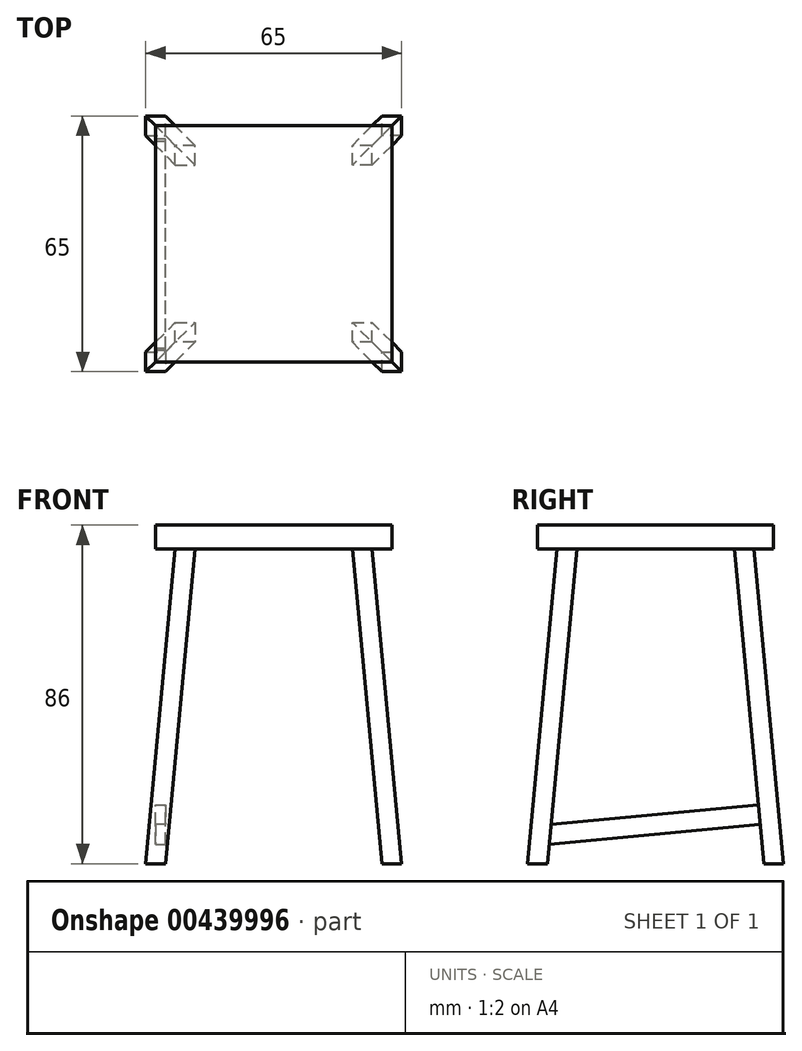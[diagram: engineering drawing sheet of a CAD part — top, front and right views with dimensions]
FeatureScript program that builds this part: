
annotation { "Feature Type Name" : "Feature", "Feature Type Description" : "" }
export const myFeature = defineFeature(function(context is Context, id is Id, definition is map)
    precondition{}
    {
        {
            var Q0;
            Q0=qCreatedBy(makeId("Top.planeOp"),FACE);
            var sketch = newSketch(context, id + "F0", { "sketchPlane" : qUnion([Q0])});
            skLineSegment(sketch, "E0.bottom", {"start": v(30, 30) * mm, "end": v(-30, 30) * mm});
            skLineSegment(sketch, "E0.top", {"start": v(30, -30) * mm, "end": v(-30, -30) * mm});
            skLineSegment(sketch, "E0.left", {"start": v(30, 30) * mm, "end": v(30, -30) * mm});
            skLineSegment(sketch, "E0.right", {"start": v(-30, 30) * mm, "end": v(-30, -30) * mm});
            skPoint(sketch, "E0.middle", {"position": v(0, 0) * mm});
            skSolve(sketch);
        }
        {
            var Q0;
            Q0=makeQuery(id+"F0.imprint","IMPRINT",FACE,{"disambiguationData":[TD([[makeQuery(id+"F0.imprint","IMPRINT",EDGE,{"derivedFrom":sQuery(id+"F0.wireOp",EDGE,"E0.bottom")}),1.0]])]});
            extrude(context, id + "F1", {"entities" : qUnion([Q0]), "depth" : 6 * mm});
        }
        {
            var Q0;
            Q0=makeQuery(id+"F1.opExtrude","CAP_FACE",FACE,{"disambiguationData":[OSD([sQuery(id+"F0.wireOp",EDGE,"E0.bottom"),sQuery(id+"F0.wireOp",EDGE,"E0.top"),sQuery(id+"F0.wireOp",EDGE,"E0.left"),sQuery(id+"F0.wireOp",EDGE,"E0.right")])],"isStart":true});
            var sketch = newSketch(context, id + "F2", { "sketchPlane" : qUnion([Q0])});
            skLineSegment(sketch, "E1.bottom", {"start": v(25, 25) * mm, "end": v(-25, 25) * mm});
            skLineSegment(sketch, "E1.top", {"start": v(25, -25) * mm, "end": v(-25, -25) * mm});
            skLineSegment(sketch, "E1.left", {"start": v(25, 25) * mm, "end": v(25, -25) * mm});
            skLineSegment(sketch, "E1.right", {"start": v(-25, 25) * mm, "end": v(-25, -25) * mm});
            skPoint(sketch, "E1.middle", {"position": v(0, 0) * mm});
            skLineSegment(sketch, "E2", {"start": v(-20, 25) * mm, "end": v(-20, 20) * mm});
            skLineSegment(sketch, "E3", {"start": v(-20, 20) * mm, "end": v(-25, 20) * mm});
            skLineSegment(sketch, "E4", {"start": v(-25, -20) * mm, "end": v(-20, -20) * mm});
            skLineSegment(sketch, "E5", {"start": v(-20, -20) * mm, "end": v(-20, -25) * mm});
            skLineSegment(sketch, "E6", {"start": v(25, 20) * mm, "end": v(20, 20) * mm});
            skLineSegment(sketch, "E7", {"start": v(20, 20) * mm, "end": v(20, 25) * mm});
            skLineSegment(sketch, "E8", {"start": v(25, -20) * mm, "end": v(20, -20) * mm});
            skLineSegment(sketch, "E9", {"start": v(20, -20) * mm, "end": v(20, -25) * mm});
            skSolve(sketch);
        }
        {
            var Q0;
            Q0=qCreatedBy(makeId("Top.planeOp"),FACE);
            cPlane(context, id + "F3", {"entities" : qUnion([Q0]), "cplaneType" : CPlaneType.OFFSET, "offset" : 80 * mm, "oppositeDirection" : true, "width" : 150 * mm, "height" : 150 * mm});
        }
        {
            var Q0;
            Q0=qCreatedBy(id+"F3.planeOp",FACE);
            var sketch = newSketch(context, id + "F4", { "sketchPlane" : qUnion([Q0])});
            skLineSegment(sketch, "E10.bottom", {"start": v(-32.5, 32.5) * mm, "end": v(32.5, 32.5) * mm});
            skLineSegment(sketch, "E10.top", {"start": v(-32.5, -32.5) * mm, "end": v(32.5, -32.5) * mm});
            skLineSegment(sketch, "E10.left", {"start": v(-32.5, 32.5) * mm, "end": v(-32.5, -32.5) * mm});
            skLineSegment(sketch, "E10.right", {"start": v(32.5, 32.5) * mm, "end": v(32.5, -32.5) * mm});
            skPoint(sketch, "E10.middle", {"position": v(0, 0) * mm});
            skLineSegment(sketch, "E11", {"start": v(27.5, 32.5) * mm, "end": v(27.5, 27.5) * mm});
            skLineSegment(sketch, "E12", {"start": v(27.5, 27.5) * mm, "end": v(32.5, 27.5) * mm});
            skLineSegment(sketch, "E13", {"start": v(32.5, -27.5) * mm, "end": v(27.5, -27.5) * mm});
            skLineSegment(sketch, "E14", {"start": v(27.5, -27.5) * mm, "end": v(27.5, -32.5) * mm});
            skLineSegment(sketch, "E15", {"start": v(-32.5, -27.5) * mm, "end": v(-27.5, -27.5) * mm});
            skLineSegment(sketch, "E16", {"start": v(-27.5, -27.5) * mm, "end": v(-27.5, -32.5) * mm});
            skLineSegment(sketch, "E17", {"start": v(-32.5, 27.5) * mm, "end": v(-27.5, 27.5) * mm});
            skLineSegment(sketch, "E18", {"start": v(-27.5, 27.5) * mm, "end": v(-27.5, 32.5) * mm});
            skSolve(sketch);
        }
        {
            var Q1;
            {var subQ4=sQuery(id+"F2.wireOp",EDGE,"E4");Q1=makeQuery(id+"F2.imprint","IMPRINT",FACE,{"disambiguationData":[TD([[makeQuery(id+"F2.imprint","IMPRINT",EDGE,{"derivedFrom":subQ4}),-1.0]])]});}
            var Q2;
            {var subQ4=sQuery(id+"F4.wireOp",EDGE,"E17");Q2=makeQuery(id+"F4.imprint","IMPRINT",FACE,{"disambiguationData":[TD([[makeQuery(id+"F4.imprint","IMPRINT",EDGE,{"derivedFrom":subQ4}),1.0]])]});}
            loft(context, id + "F5", {"operationType" : NewBodyOperationType.ADD, "sheetProfilesArray" : [{ "sheetProfileEntities" : qUnion([Q1]) }, { "sheetProfileEntities" : qUnion([Q2]) }]});
        }
        {
            var Q0;
            Q0=makeQuery(id+"F1.opExtrude","CAP_FACE",FACE,{"disambiguationData":[OSD([sQuery(id+"F0.wireOp",EDGE,"E0.bottom"),sQuery(id+"F0.wireOp",EDGE,"E0.top"),sQuery(id+"F0.wireOp",EDGE,"E0.left"),sQuery(id+"F0.wireOp",EDGE,"E0.right")])],"isStart":true});
            var sketch = newSketch(context, id + "F6", { "sketchPlane" : qUnion([Q0])});
            skLineSegment(sketch, "E19.bottom", {"start": v(25, 25) * mm, "end": v(-25, 25) * mm});
            skLineSegment(sketch, "E19.top", {"start": v(25, -25) * mm, "end": v(-25, -25) * mm});
            skLineSegment(sketch, "E19.left", {"start": v(25, 25) * mm, "end": v(25, -25) * mm});
            skLineSegment(sketch, "E19.right", {"start": v(-25, 25) * mm, "end": v(-25, -25) * mm});
            skPoint(sketch, "E19.middle", {"position": v(0, 0) * mm});
            skLineSegment(sketch, "E20", {"start": v(-25, 20) * mm, "end": v(-20, 20) * mm});
            skLineSegment(sketch, "E21", {"start": v(-20, 20) * mm, "end": v(-20, 25) * mm});
            skSolve(sketch);
        }
        {
            var Q0;
            Q0=qCreatedBy(id+"F3.planeOp",FACE);
            var sketch = newSketch(context, id + "F7", { "sketchPlane" : qUnion([Q0])});
            skLineSegment(sketch, "E22.bottom", {"start": v(32.5, -32.5) * mm, "end": v(-32.5, -32.5) * mm});
            skLineSegment(sketch, "E22.top", {"start": v(32.5, 32.5) * mm, "end": v(-32.5, 32.5) * mm});
            skLineSegment(sketch, "E22.left", {"start": v(32.5, -32.5) * mm, "end": v(32.5, 32.5) * mm});
            skLineSegment(sketch, "E22.right", {"start": v(-32.5, -32.5) * mm, "end": v(-32.5, 32.5) * mm});
            skPoint(sketch, "E22.middle", {"position": v(0, 0) * mm});
            skLineSegment(sketch, "E23", {"start": v(-32.5, -27.5) * mm, "end": v(-27.5, -27.5) * mm});
            skLineSegment(sketch, "E24", {"start": v(-27.5, -27.5) * mm, "end": v(-27.5, -32.5) * mm});
            skSolve(sketch);
        }
        {
            var Q1;
            {var subQ4=sQuery(id+"F7.wireOp",EDGE,"E23");Q1=makeQuery(id+"F7.imprint","IMPRINT",FACE,{"disambiguationData":[TD([[makeQuery(id+"F7.imprint","IMPRINT",EDGE,{"derivedFrom":subQ4}),-1.0]])]});}
            var Q2;
            {var subQ4=sQuery(id+"F6.wireOp",EDGE,"E20");Q2=makeQuery(id+"F6.imprint","IMPRINT",FACE,{"disambiguationData":[TD([[makeQuery(id+"F6.imprint","IMPRINT",EDGE,{"derivedFrom":subQ4}),1.0]])]});}
            loft(context, id + "F8", {"operationType" : NewBodyOperationType.ADD, "sheetProfilesArray" : [{ "sheetProfileEntities" : qUnion([Q1]) }, { "sheetProfileEntities" : qUnion([Q2]) }]});
        }
        {
            var Q0;
            Q0=qCreatedBy(id+"F3.planeOp",FACE);
            var sketch = newSketch(context, id + "F9", { "sketchPlane" : qUnion([Q0])});
            skLineSegment(sketch, "E25.bottom", {"start": v(32.5, -32.5) * mm, "end": v(-32.5, -32.5) * mm});
            skLineSegment(sketch, "E25.top", {"start": v(32.5, 32.5) * mm, "end": v(-32.5, 32.5) * mm});
            skLineSegment(sketch, "E25.left", {"start": v(32.5, -32.5) * mm, "end": v(32.5, 32.5) * mm});
            skLineSegment(sketch, "E25.right", {"start": v(-32.5, -32.5) * mm, "end": v(-32.5, 32.5) * mm});
            skPoint(sketch, "E25.middle", {"position": v(0, 0) * mm});
            skLineSegment(sketch, "E26", {"start": v(27.5, -32.5) * mm, "end": v(27.5, -27.5) * mm});
            skLineSegment(sketch, "E27", {"start": v(27.5, -27.5) * mm, "end": v(32.5, -27.5) * mm});
            skLineSegment(sketch, "E28", {"start": v(27.5, 32.5) * mm, "end": v(27.5, 27.5) * mm});
            skLineSegment(sketch, "E29", {"start": v(27.5, 27.5) * mm, "end": v(32.5, 27.5) * mm});
            skSolve(sketch);
        }
        {
            var Q0;
            Q0=makeQuery(id+"F1.opExtrude","CAP_FACE",FACE,{"disambiguationData":[OSD([sQuery(id+"F0.wireOp",EDGE,"E0.bottom"),sQuery(id+"F0.wireOp",EDGE,"E0.top"),sQuery(id+"F0.wireOp",EDGE,"E0.left"),sQuery(id+"F0.wireOp",EDGE,"E0.right")])],"isStart":true});
            var sketch = newSketch(context, id + "F10", { "sketchPlane" : qUnion([Q0])});
            skLineSegment(sketch, "E30.bottom", {"start": v(25, 25) * mm, "end": v(-25, 25) * mm});
            skLineSegment(sketch, "E30.top", {"start": v(25, -25) * mm, "end": v(-25, -25) * mm});
            skLineSegment(sketch, "E30.left", {"start": v(25, 25) * mm, "end": v(25, -25) * mm});
            skLineSegment(sketch, "E30.right", {"start": v(-25, 25) * mm, "end": v(-25, -25) * mm});
            skPoint(sketch, "E30.middle", {"position": v(0, 0) * mm});
            skLineSegment(sketch, "E31", {"start": v(20, 25) * mm, "end": v(20, 20) * mm});
            skLineSegment(sketch, "E32", {"start": v(20, 20) * mm, "end": v(25, 20) * mm});
            skLineSegment(sketch, "E33", {"start": v(20, -25) * mm, "end": v(20, -20) * mm});
            skLineSegment(sketch, "E34", {"start": v(20, -20) * mm, "end": v(25, -20) * mm});
            skSolve(sketch);
        }
        {
            var Q1;
            {var subQ3=sQuery(id+"F9.wireOp",EDGE,"E26");Q1=makeQuery(id+"F9.imprint","IMPRINT",FACE,{"disambiguationData":[TD([[makeQuery(id+"F9.imprint","IMPRINT",EDGE,{"derivedFrom":subQ3}),-1.0]])]});}
            var Q2;
            {var subQ3=sQuery(id+"F10.wireOp",EDGE,"E31");Q2=makeQuery(id+"F10.imprint","IMPRINT",FACE,{"disambiguationData":[TD([[makeQuery(id+"F10.imprint","IMPRINT",EDGE,{"derivedFrom":subQ3}),1.0]])]});}
            loft(context, id + "F11", {"operationType" : NewBodyOperationType.ADD, "sheetProfilesArray" : [{ "sheetProfileEntities" : qUnion([Q1]) }, { "sheetProfileEntities" : qUnion([Q2]) }]});
        }
        {
            var Q0;
            Q0=qCreatedBy(id+"F3.planeOp",FACE);
            var sketch = newSketch(context, id + "F12", { "sketchPlane" : qUnion([Q0])});
            skLineSegment(sketch, "E35.bottom", {"start": v(32.5, -32.5) * mm, "end": v(-32.5, -32.5) * mm});
            skLineSegment(sketch, "E35.top", {"start": v(32.5, 32.5) * mm, "end": v(-32.5, 32.5) * mm});
            skLineSegment(sketch, "E35.left", {"start": v(32.5, -32.5) * mm, "end": v(32.5, 32.5) * mm});
            skLineSegment(sketch, "E35.right", {"start": v(-32.5, -32.5) * mm, "end": v(-32.5, 32.5) * mm});
            skPoint(sketch, "E35.middle", {"position": v(0, 0) * mm});
            skLineSegment(sketch, "E36", {"start": v(32.5, 27.5) * mm, "end": v(27.5, 27.5) * mm});
            skLineSegment(sketch, "E37", {"start": v(27.5, 27.5) * mm, "end": v(27.5, 32.5) * mm});
            skSolve(sketch);
        }
        {
            var Q0;
            Q0=makeQuery(id+"F1.opExtrude","CAP_FACE",FACE,{"disambiguationData":[OSD([sQuery(id+"F0.wireOp",EDGE,"E0.bottom"),sQuery(id+"F0.wireOp",EDGE,"E0.top"),sQuery(id+"F0.wireOp",EDGE,"E0.left"),sQuery(id+"F0.wireOp",EDGE,"E0.right")])],"isStart":true});
            var sketch = newSketch(context, id + "F13", { "sketchPlane" : qUnion([Q0])});
            skLineSegment(sketch, "E38.bottom", {"start": v(25, 25) * mm, "end": v(-25, 25) * mm});
            skLineSegment(sketch, "E38.top", {"start": v(25, -25) * mm, "end": v(-25, -25) * mm});
            skLineSegment(sketch, "E38.left", {"start": v(25, 25) * mm, "end": v(25, -25) * mm});
            skLineSegment(sketch, "E38.right", {"start": v(-25, 25) * mm, "end": v(-25, -25) * mm});
            skPoint(sketch, "E38.middle", {"position": v(0, 0) * mm});
            skLineSegment(sketch, "E39", {"start": v(25, -20) * mm, "end": v(20, -20) * mm});
            skLineSegment(sketch, "E40", {"start": v(20, -20) * mm, "end": v(20, -25) * mm});
            skSolve(sketch);
        }
        {
            var Q1;
            {var subQ4=sQuery(id+"F12.wireOp",EDGE,"E36");Q1=makeQuery(id+"F12.imprint","IMPRINT",FACE,{"disambiguationData":[TD([[makeQuery(id+"F12.imprint","IMPRINT",EDGE,{"derivedFrom":subQ4}),-1.0]])]});}
            var Q2;
            {var subQ4=sQuery(id+"F13.wireOp",EDGE,"E39");Q2=makeQuery(id+"F13.imprint","IMPRINT",FACE,{"disambiguationData":[TD([[makeQuery(id+"F13.imprint","IMPRINT",EDGE,{"derivedFrom":subQ4}),1.0]])]});}
            loft(context, id + "F14", {"operationType" : NewBodyOperationType.ADD, "sheetProfilesArray" : [{ "sheetProfileEntities" : qUnion([Q1]) }, { "sheetProfileEntities" : qUnion([Q2]) }]});
        }
        {
            var Q0;
            Q0=makeQuery(id+"F5.opLoft","SWEPT_FACE",FACE,{"disambiguationData":[OSD([sQuery(id+"F2.wireOp",EDGE,"E1.right"),sQuery(id+"F2.wireOp",EDGE,"E4"),sQuery(id+"F2.wireOp",EDGE,"E5"),sQuery(id+"F4.wireOp",EDGE,"E10.left"),sQuery(id+"F4.wireOp",EDGE,"E17"),sQuery(id+"F4.wireOp",EDGE,"E18")])]});
            var sketch = newSketch(context, id + "F15", { "sketchPlane" : qUnion([Q0])});
            skLineSegment(sketch, "E41.0.0", {"start": v(-32.5, -77.08) * mm, "end": v(-25, 1.87) * mm});
            skLineSegment(sketch, "E41.0.1", {"start": v(-20, 1.87) * mm, "end": v(-25, 1.87) * mm});
            skLineSegment(sketch, "E41.0.2", {"start": v(-20, 1.87) * mm, "end": v(-27.5, -77.08) * mm});
            skLineSegment(sketch, "E41.0.3", {"start": v(-27.5, -77.08) * mm, "end": v(-32.5, -77.08) * mm});
            skLineSegment(sketch, "E42", {"start": v(-30, -72.22) * mm, "end": v(-30, -67.22) * mm});
            skLineSegment(sketch, "E43", {"start": v(-30, -67.22) * mm, "end": v(-27.5, -67.22) * mm});
            skLineSegment(sketch, "E44", {"start": v(-27.5, -67.22) * mm, "end": v(-27.5, -72.22) * mm});
            skLineSegment(sketch, "E45", {"start": v(-27.5, -72.22) * mm, "end": v(-30, -72.22) * mm});
            skSolve(sketch);
        }
        {
            var Q0;
            Q0=makeQuery(id+"F15.imprint","IMPRINT",FACE,{"disambiguationData":[TD([[makeQuery(id+"F15.imprint","IMPRINT",EDGE,{"derivedFrom":sQuery(id+"F15.wireOp",EDGE,"E42")}),-1.0]])]});
            extrude(context, id + "F16", {"entities" : qUnion([Q0]), "operationType" : NewBodyOperationType.ADD, "depth" : 55 * mm});
        }
    });
